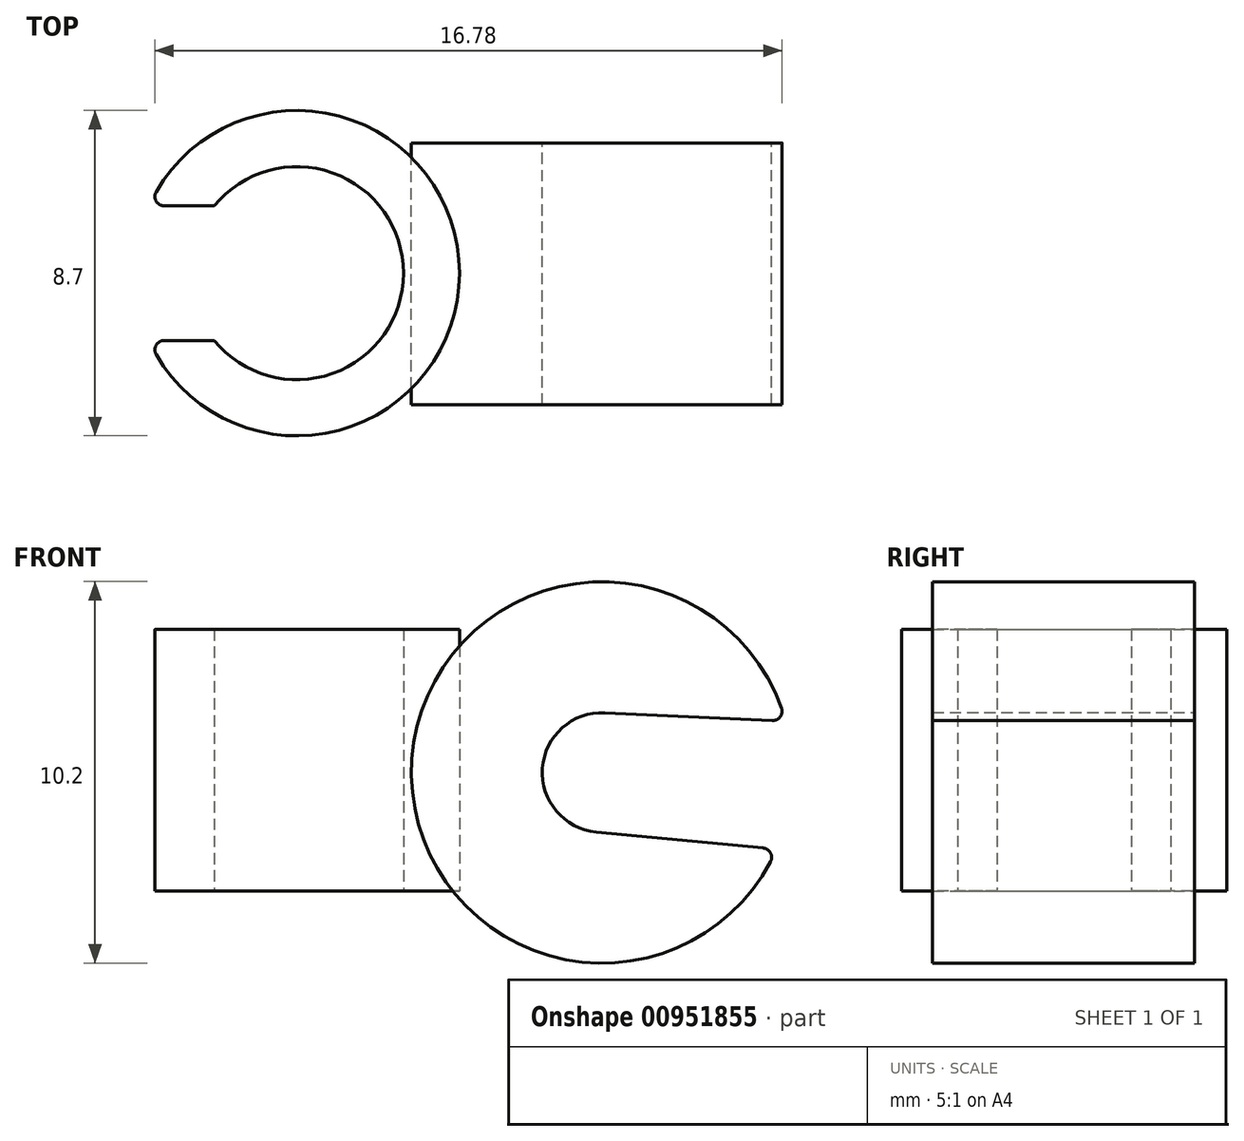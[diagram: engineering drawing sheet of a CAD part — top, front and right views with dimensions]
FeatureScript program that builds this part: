
annotation { "Feature Type Name" : "Feature", "Feature Type Description" : "" }
export const myFeature = defineFeature(function(context is Context, id is Id, definition is map)
    precondition{}
    {
        {
            var Q0;
            Q0=qCreatedBy(makeId("Top.planeOp"),FACE);
            var sketch = newSketch(context, id + "F0", { "sketchPlane" : qUnion([Q0])});
            skCircle(sketch, "E0", {"center": v(-49.26, 11.22) * mm, "radius": 2.85 * mm});
            skCircle(sketch, "E1.0", {"center": v(-49.26, 11.22) * mm, "radius": 4.35 * mm});
            skLineSegment(sketch, "E2.0", {"start": v(-49.26, 9.42) * mm, "end": v(-40.83, 9.42) * mm});
            skLineSegment(sketch, "E3.0", {"start": v(-49.26, 13.02) * mm, "end": v(-40.83, 13.02) * mm});
            skSolve(sketch);
        }
        {
            var Q0;
            {var subQ0=sQuery(id+"F0.wireOp",EDGE,"E2.0");var subQ1=sQuery(id+"F0.wireOp",EDGE,"E0");var subQ2=makeQuery(id+"F0.imprint","INTERSECT",VERTEX,{"derivedFrom":[subQ1,subQ0]});Q0=makeQuery(id+"F0.imprint","IMPRINT",FACE,{"disambiguationData":[TD([[makeQuery(id+"F0.imprint","IMPRINT",EDGE,{"disambiguationData":[TD([[subQ2,1.0]])],"derivedFrom":subQ1}),-1.0]])]});}
            extrude(context, id + "F1", {"entities" : qUnion([Q0]), "depth" : 3 * mm, "offsetDistance" : 25 * mm});
        }
        {
            var Q0;
            Q0=qCreatedBy(makeId("Front.planeOp"),FACE);
            var sketch = newSketch(context, id + "F2", { "sketchPlane" : qUnion([Q0])});
            skCircle(sketch, "E4", {"center": v(-51.18, 11.38) * mm, "radius": 1.6 * mm});
            skCircle(sketch, "E5.0", {"center": v(-51.18, 11.38) * mm, "radius": 5.1 * mm});
            skLineSegment(sketch, "E6", {"start": v(-51.6, 9.83) * mm, "end": v(-44.95, 8) * mm});
            skLineSegment(sketch, "E7", {"start": v(-50.82, 12.94) * mm, "end": v(-43.88, 11.38) * mm});
            skSolve(sketch);
        }
        {
            var Q0;
            {var subQ0=sQuery(id+"F2.wireOp",EDGE,"E6");var subQ1=sQuery(id+"F2.wireOp",EDGE,"E4");var subQ2=makeQuery(id+"F2.imprint","INTERSECT",VERTEX,{"derivedFrom":[subQ1,subQ0]});Q0=makeQuery(id+"F2.imprint","IMPRINT",FACE,{"disambiguationData":[TD([[makeQuery(id+"F2.imprint","IMPRINT",EDGE,{"disambiguationData":[TD([[subQ2,1.0]])],"derivedFrom":subQ1}),-1.0]])]});}
            extrude(context, id + "F3", {"entities" : qUnion([Q0]), "depth" : 7 * mm, "offsetDistance" : 25 * mm});
        }
        {
            var Q0;
            Q0=makeQuery(id+"F1.opExtrude","SWEPT_EDGE",EDGE,{"disambiguationData":[OSD([sQuery(id+"F0.wireOp",EDGE,"E1.0"),sQuery(id+"F0.wireOp",EDGE,"E2.0")])]});
            fillet(context, id + "F4", {"entities" : qUnion([Q0]), "radius" : .25 * mm, "tangentPropagation" : true, "allowEdgeOverflow" : false});
        }
        {
            var Q0;
            Q0=makeQuery(id+"F1.opExtrude","SWEPT_EDGE",EDGE,{"disambiguationData":[OSD([sQuery(id+"F0.wireOp",EDGE,"E1.0"),sQuery(id+"F0.wireOp",EDGE,"E3.0")])]});
            fillet(context, id + "F5", {"entities" : qUnion([Q0]), "radius" : .25 * mm, "tangentPropagation" : true, "allowEdgeOverflow" : false});
        }
        {
            var Q0;
            Q0=makeQuery(id+"F3.opExtrude","SWEPT_EDGE",EDGE,{"disambiguationData":[OSD([sQuery(id+"F2.wireOp",EDGE,"E5.0"),sQuery(id+"F2.wireOp",EDGE,"E7")])]});
            fillet(context, id + "F6", {"entities" : qUnion([Q0]), "radius" : .25 * mm, "tangentPropagation" : true, "allowEdgeOverflow" : false});
        }
        {
            var Q0;
            Q0=makeQuery(id+"F3.opExtrude","SWEPT_EDGE",EDGE,{"disambiguationData":[OSD([sQuery(id+"F2.wireOp",EDGE,"E5.0"),sQuery(id+"F2.wireOp",EDGE,"E6")])]});
            fillet(context, id + "F7", {"entities" : qUnion([Q0]), "radius" : .25 * mm, "tangentPropagation" : true, "allowEdgeOverflow" : false});
        }
        {
            var Q0;
            Q0=makeQuery(id+"F3.opExtrude","SWEPT_BODY",BODY,{"disambiguationData":[OSD([sQuery(id+"F2.wireOp",EDGE,"E4"),sQuery(id+"F2.wireOp",EDGE,"E5.0"),sQuery(id+"F2.wireOp",EDGE,"E6"),sQuery(id+"F2.wireOp",EDGE,"E7")])]});
            var Q1;
            Q1=makeQuery(id+"F3.opExtrude","CAP_EDGE",EDGE,{"disambiguationData":[OSD([sQuery(id+"F2.wireOp",EDGE,"E5.0")])],"isStart":false});
            transform(context, id + "F8", {"entities" : qUnion([Q0]), "transformType" : TransformType.ROTATION, "transformAxis" : qUnion([Q1]), "angle" : 10 * degree, "makeCopy" : false});
        }
        {
            var Q0;
            Q0=makeQuery(id+"F1.opExtrude","SWEPT_BODY",BODY,{"disambiguationData":[OSD([sQuery(id+"F0.wireOp",EDGE,"E0"),sQuery(id+"F0.wireOp",EDGE,"E1.0"),sQuery(id+"F0.wireOp",EDGE,"E2.0"),sQuery(id+"F0.wireOp",EDGE,"E3.0")])]});
            var Q1;
            Q1=makeQuery(id+"F1.opExtrude","CAP_EDGE",EDGE,{"disambiguationData":[OSD([sQuery(id+"F0.wireOp",EDGE,"E0")])],"isStart":true});
            transform(context, id + "F9", {"entities" : qUnion([Q0]), "transformType" : TransformType.ROTATION, "transformAxis" : qUnion([Q1]), "angle" : 180 * degree, "makeCopy" : false});
        }
        {
            var Q0;
            Q0=makeQuery(id+"F1.opExtrude","SWEPT_BODY",BODY,{"disambiguationData":[OSD([sQuery(id+"F0.wireOp",EDGE,"E0"),sQuery(id+"F0.wireOp",EDGE,"E1.0"),sQuery(id+"F0.wireOp",EDGE,"E2.0"),sQuery(id+"F0.wireOp",EDGE,"E3.0")])]});
            var Q1;
            Q1=qCreatedBy(makeId("Top.planeOp"),FACE);
            transform(context, id + "F10", {"entities" : qUnion([Q0]), "transformType" : TransformType.TRANSLATION_DISTANCE, "transformDirection" : qUnion([Q1]), "distance" : 11.1 * mm, "makeCopy" : false});
        }
        {
            var Q0;
            Q0=makeQuery(id+"F1.opExtrude","SWEPT_BODY",BODY,{"disambiguationData":[OSD([sQuery(id+"F0.wireOp",EDGE,"E0"),sQuery(id+"F0.wireOp",EDGE,"E1.0"),sQuery(id+"F0.wireOp",EDGE,"E2.0"),sQuery(id+"F0.wireOp",EDGE,"E3.0")])]});
            var Q1;
            Q1=makeQuery(id+"F3.opExtrude","SWEPT_FACE",FACE,{"disambiguationData":[OSD([sQuery(id+"F2.wireOp",EDGE,"E5.0")])]});
            transform(context, id + "F11", {"entities" : qUnion([Q0]), "transformType" : TransformType.TRANSLATION_DISTANCE, "transformDirection" : qUnion([Q1]), "distance" : 14.7 * mm, "oppositeDirection" : true, "makeCopy" : false});
        }
        {
            var Q0;
            Q0=makeQuery(id+"F3.opExtrude","SWEPT_BODY",BODY,{"disambiguationData":[OSD([sQuery(id+"F2.wireOp",EDGE,"E4"),sQuery(id+"F2.wireOp",EDGE,"E5.0"),sQuery(id+"F2.wireOp",EDGE,"E6"),sQuery(id+"F2.wireOp",EDGE,"E7")])]});
            transform(context, id + "F12", {"entities" : qUnion([Q0]), "transformType" : TransformType.TRANSLATION_3D, "dx" : 9.9 * mm, "dy" : 0 * mm, "dz" : 0 * mm, "makeCopy" : false});
        }
        {
            var Q0;
            Q0=makeQuery(id+"F1.opExtrude","SWEPT_BODY",BODY,{"disambiguationData":[OSD([sQuery(id+"F0.wireOp",EDGE,"E0"),sQuery(id+"F0.wireOp",EDGE,"E1.0"),sQuery(id+"F0.wireOp",EDGE,"E2.0"),sQuery(id+"F0.wireOp",EDGE,"E3.0")])]});
            transform(context, id + "F13", {"entities" : qUnion([Q0]), "transformType" : TransformType.TRANSLATION_3D, "dx" : -1.43 * mm, "dy" : 0 * mm, "dz" : 0 * mm, "makeCopy" : false});
        }
        {
            var Q0;
            Q0=makeQuery(id+"F1.opExtrude","SWEPT_BODY",BODY,{"disambiguationData":[OSD([sQuery(id+"F0.wireOp",EDGE,"E0"),sQuery(id+"F0.wireOp",EDGE,"E1.0"),sQuery(id+"F0.wireOp",EDGE,"E2.0"),sQuery(id+"F0.wireOp",EDGE,"E3.0")])]});
            var Q1;
            Q1=makeQuery(id+"F1.opExtrude","SWEPT_FACE",FACE,{"disambiguationData":[OSD([sQuery(id+"F0.wireOp",EDGE,"E1.0")])]});
            var Q2;
            Q2=qCreatedBy(makeId("Front.planeOp"),FACE);
            transform(context, id + "F14", {"entities" : qUnion([Q0]), "transformType" : TransformType.TRANSLATION_DISTANCE, "transformDirection" : qUnion([Q1, Q2]), "distance" : 1.2 * mm, "makeCopy" : false});
        }
        {
            var Q0;
            Q0=makeQuery(id+"F1.opExtrude","CAP_FACE",FACE,{"disambiguationData":[OSD([sQuery(id+"F0.wireOp",EDGE,"E0"),sQuery(id+"F0.wireOp",EDGE,"E1.0"),sQuery(id+"F0.wireOp",EDGE,"E2.0"),sQuery(id+"F0.wireOp",EDGE,"E3.0")])],"isStart":false});
            extrude(context, id + "F15", {"entities" : qUnion([Q0]), "operationType" : NewBodyOperationType.ADD, "depth" : 4 * mm, "offsetDistance" : 25 * mm});
        }
        {
            var Q0;
            Q0=makeQuery(id+"F3.opExtrude","SWEPT_BODY",BODY,{"disambiguationData":[OSD([sQuery(id+"F2.wireOp",EDGE,"E4"),sQuery(id+"F2.wireOp",EDGE,"E5.0"),sQuery(id+"F2.wireOp",EDGE,"E6"),sQuery(id+"F2.wireOp",EDGE,"E7")])]});
            transform(context, id + "F16", {"entities" : qUnion([Q0]), "transformType" : TransformType.TRANSLATION_3D, "dx" : 0 * mm, "dy" : 0 * mm, "dz" : 1.7 * mm, "makeCopy" : false});
        }
        {
            var Q0;
            Q0=makeQuery(id+"F1.opExtrude","SWEPT_BODY",BODY,{"disambiguationData":[OSD([sQuery(id+"F0.wireOp",EDGE,"E0"),sQuery(id+"F0.wireOp",EDGE,"E1.0"),sQuery(id+"F0.wireOp",EDGE,"E2.0"),sQuery(id+"F0.wireOp",EDGE,"E3.0")])]});
            transform(context, id + "F17", {"entities" : qUnion([Q0]), "transformType" : TransformType.TRANSLATION_3D, "dx" : 1.25 * mm, "dy" : 0 * mm, "dz" : 0 * mm, "makeCopy" : false});
        }
    });
